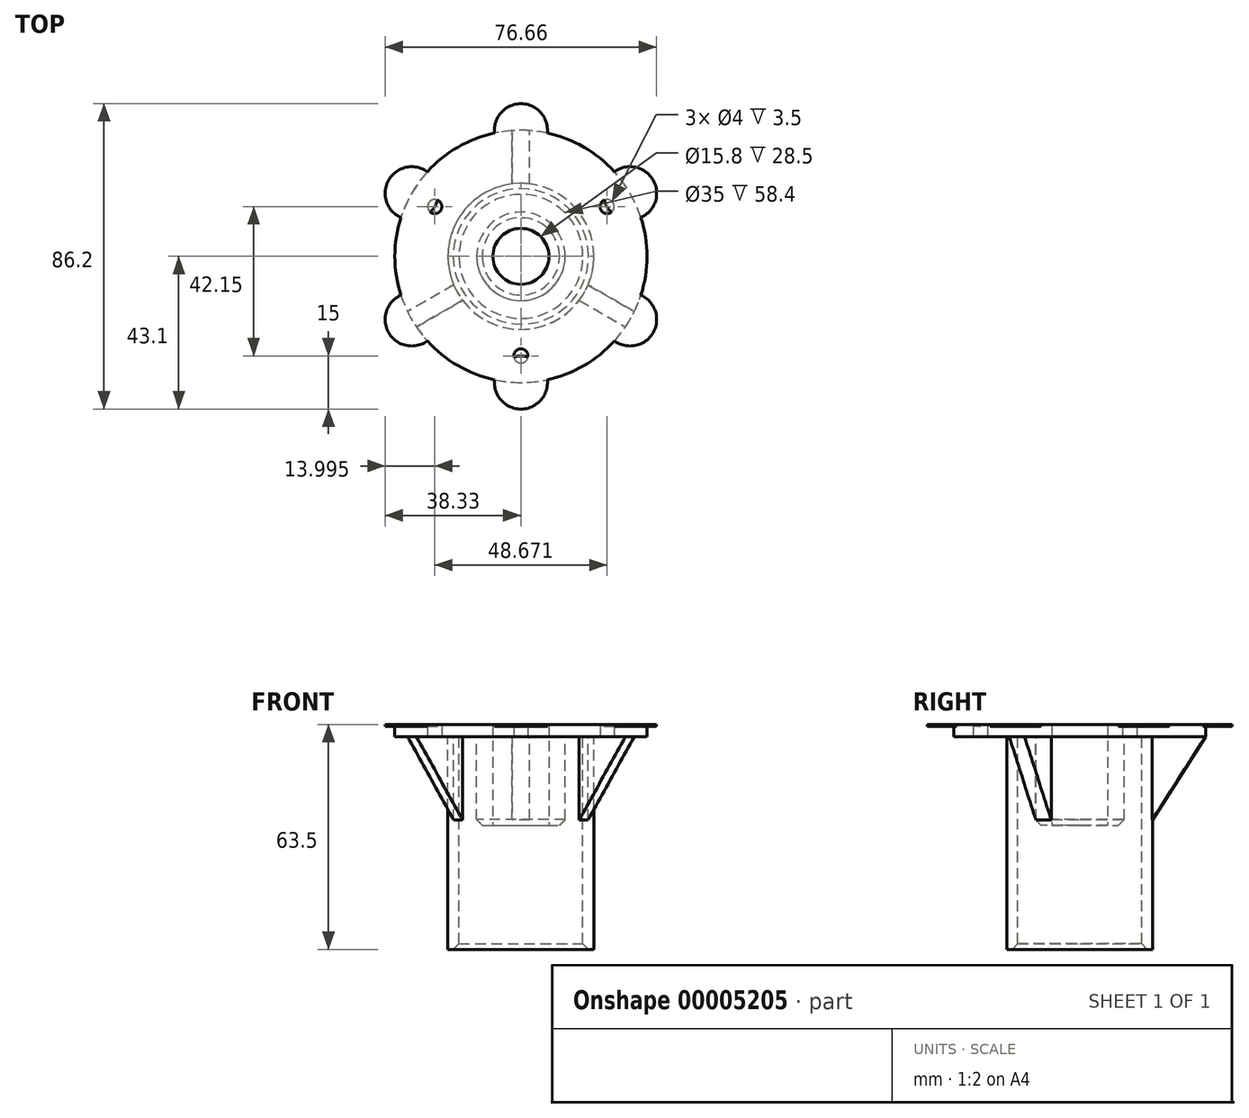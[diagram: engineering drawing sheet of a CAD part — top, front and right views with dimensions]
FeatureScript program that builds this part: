
annotation { "Feature Type Name" : "Feature", "Feature Type Description" : "" }
export const myFeature = defineFeature(function(context is Context, id is Id, definition is map)
    precondition{}
    {
        {
            var Q0;
            Q0=qCreatedBy(makeId("Front.planeOp"),FACE);
            var sketch = newSketch(context, id + "F0", { "sketchPlane" : qUnion([Q0])});
            skLineSegment(sketch, "E0", {"start": v(0, 36.77) * mm, "end": v(0, 0) * mm, "construction": true});
            skLineSegment(sketch, "E1", {"start": v(0, 0) * mm, "end": v(35.6, 0) * mm});
            skLineSegment(sketch, "E2", {"start": v(35.6, 0) * mm, "end": v(35.6, -3.5) * mm});
            skLineSegment(sketch, "E3", {"start": v(35.6, -3.5) * mm, "end": v(20.6, -3.5) * mm});
            skLineSegment(sketch, "E4", {"start": v(20.6, -3.5) * mm, "end": v(20.6, -63.5) * mm});
            skLineSegment(sketch, "E5", {"start": v(20.6, -63.5) * mm, "end": v(17.1, -63.5) * mm});
            skLineSegment(sketch, "E6", {"start": v(17.1, -63.5) * mm, "end": v(17.1, -3.5) * mm});
            skLineSegment(sketch, "E7", {"start": v(17.1, -3.5) * mm, "end": v(12.9, -3.5) * mm});
            skLineSegment(sketch, "E8", {"start": v(12.9, -3.5) * mm, "end": v(12.9, -28.5) * mm});
            skLineSegment(sketch, "E9", {"start": v(12.9, -28.5) * mm, "end": v(0, -28.5) * mm});
            skLineSegment(sketch, "E10", {"start": v(0, -28.5) * mm, "end": v(0, 0) * mm});
            skLineSegment(sketch, "E11", {"start": v(28.1, -3.5) * mm, "end": v(28.1, 0) * mm, "construction": true});
            skSolve(sketch);
        }
        {
            var Q0;
            Q0 = qSketchRegion(id + "F0", true);
            var Q1;
            Q1=sQuery(id+"F0.wireOp",EDGE,"E0");
            revolve(context, id + "F1", {"entities" : qUnion([Q0]), "axis" : qUnion([Q1]), "revolveType" : RevolveType.FULL});
        }
        {
            var Q0;
            Q0=makeQuery(id+"F1.opRevolve","SWEPT_EDGE",EDGE,{"disambiguationData":[OSD([sQuery(id+"F0.wireOp",EDGE,"E8"),sQuery(id+"F0.wireOp",EDGE,"E9")])]});
            var Q1;
            Q1=makeQuery(id+"F1.opRevolve","SWEPT_EDGE",EDGE,{"disambiguationData":[OSD([sQuery(id+"F0.wireOp",EDGE,"E5"),sQuery(id+"F0.wireOp",EDGE,"E6")])]});
            chamfer(context, id + "F2", {"entities" : qUnion([Q0, Q1]), "width" : 2 * mm, "tangentPropagation" : true});
        }
        {
            var Q0;
            Q0=makeQuery(id+"F1.opRevolve","SWEPT_FACE",FACE,{"disambiguationData":[OSD([sQuery(id+"F0.wireOp",EDGE,"E9")])]});
            var sketch = newSketch(context, id + "F3", { "sketchPlane" : qUnion([Q0])});
            skCircle(sketch, "E12", {"center": v(0, 0) * mm, "radius": 7.9 * mm});
            skSolve(sketch);
        }
        {
            var Q0;
            Q0 = qSketchRegion(id + "F3", true);
            extrude(context, id + "F4", {"entities" : qUnion([Q0]), "operationType" : NewBodyOperationType.REMOVE, "endBound" : BoundingType.THROUGH_ALL, "oppositeDirection" : true, "depth" : 25 * mm, "offsetDistance" : 25 * mm});
        }
        {
            var Q0;
            Q0=makeQuery(id+"F1.opRevolve","SWEPT_FACE",FACE,{"disambiguationData":[OSD([sQuery(id+"F0.wireOp",EDGE,"E3")])]});
            var sketch = newSketch(context, id + "F5", { "sketchPlane" : qUnion([Q0])});
            skLineSegment(sketch, "E13", {"start": v(0, 0) * mm, "end": v(0, 35.6) * mm, "construction": true});
            skCircle(sketch, "E14", {"center": v(0, 28.1) * mm, "radius": 2 * mm});
            skCircle(sketch, "E15.1.0", {"center": v(-24.34, -14.05) * mm, "radius": 2 * mm});
            skCircle(sketch, "E15.2.0", {"center": v(24.34, -14.05) * mm, "radius": 2 * mm});
            skPoint(sketch, "E15.center", {"position": v(0, 0) * mm});
            skSolve(sketch);
        }
        {
            var Q0;
            Q0 = qSketchRegion(id + "F5", true);
            extrude(context, id + "F6", {"entities" : qUnion([Q0]), "operationType" : NewBodyOperationType.REMOVE, "endBound" : BoundingType.THROUGH_ALL, "oppositeDirection" : true, "depth" : 25 * mm, "offsetDistance" : 25 * mm});
        }
        {
            var Q0;
            Q0=makeQuery(id+"F1.opRevolve","SWEPT_FACE",FACE,{"disambiguationData":[OSD([sQuery(id+"F0.wireOp",EDGE,"E3")])]});
            var sketch = newSketch(context, id + "F7", { "sketchPlane" : qUnion([Q0])});
            skCircle(sketch, "E16.0", {"center": v(0, 0) * mm, "radius": 20.6 * mm, "construction": true});
            skCircle(sketch, "E16.1", {"center": v(0, 0) * mm, "radius": 35.6 * mm, "construction": true});
            skLineSegment(sketch, "E17", {"start": v(0, 35.6) * mm, "end": v(0, 20.6) * mm, "construction": true});
            skLineSegment(sketch, "E18", {"start": v(0, -20.6) * mm, "end": v(0, -35.6) * mm, "construction": true});
            skLineSegment(sketch, "E19.bottom", {"start": v(-2.5, -20.45) * mm, "end": v(2.5, -20.45) * mm});
            skLineSegment(sketch, "E19.top", {"start": v(-2.5, -35.51) * mm, "end": v(2.5, -35.51) * mm, "construction": true});
            skLineSegment(sketch, "E19.left", {"start": v(-2.5, -20.45) * mm, "end": v(-2.5, -35.51) * mm});
            skLineSegment(sketch, "E19.right", {"start": v(2.5, -20.45) * mm, "end": v(2.5, -35.51) * mm});
            skArc(sketch, "E20", {"start": v(-2.5, -35.51) * mm, "mid": v(0, -35.6) * mm, "end": v(2.5, -35.51) * mm});
            skLineSegment(sketch, "E21.1.0", {"start": v(18.96, 8.06) * mm, "end": v(16.46, 12.39) * mm});
            skLineSegment(sketch, "E21.1.1", {"start": v(18.96, 8.06) * mm, "end": v(32, 15.6) * mm});
            skLineSegment(sketch, "E21.1.2", {"start": v(16.46, 12.39) * mm, "end": v(29.5, 19.92) * mm});
            skArc(sketch, "E21.1.3", {"start": v(32, 15.6) * mm, "mid": v(30.83, 17.8) * mm, "end": v(29.5, 19.92) * mm});
            skLineSegment(sketch, "E21.1.4", {"start": v(32, 15.6) * mm, "end": v(29.5, 19.92) * mm, "construction": true});
            skLineSegment(sketch, "E21.2.0", {"start": v(-16.46, 12.39) * mm, "end": v(-18.96, 8.06) * mm});
            skLineSegment(sketch, "E21.2.1", {"start": v(-16.46, 12.39) * mm, "end": v(-29.5, 19.92) * mm});
            skLineSegment(sketch, "E21.2.2", {"start": v(-18.96, 8.06) * mm, "end": v(-32, 15.6) * mm});
            skArc(sketch, "E21.2.3", {"start": v(-29.5, 19.92) * mm, "mid": v(-30.83, 17.8) * mm, "end": v(-32, 15.6) * mm});
            skLineSegment(sketch, "E21.2.4", {"start": v(-29.5, 19.92) * mm, "end": v(-32, 15.6) * mm, "construction": true});
            skSolve(sketch);
        }
        {
            var Q0;
            Q0 = qSketchRegion(id + "F7", true);
            extrude(context, id + "F8", {"entities" : qUnion([Q0]), "operationType" : NewBodyOperationType.ADD, "depth" : 25 * mm, "offsetDistance" : 25 * mm});
        }
        {
            var Q0;
            Q0=makeQuery(id+"F8.opExtrude","CAP_EDGE",EDGE,{"disambiguationData":[OSD([sQuery(id+"F7.wireOp",EDGE,"E21.2.3")])],"isStart":false});
            var Q1;
            Q1=makeQuery(id+"F8.opExtrude","CAP_EDGE",EDGE,{"disambiguationData":[OSD([sQuery(id+"F7.wireOp",EDGE,"E20")])],"isStart":false});
            var Q2;
            Q2=makeQuery(id+"F8.opExtrude","CAP_EDGE",EDGE,{"disambiguationData":[OSD([sQuery(id+"F7.wireOp",EDGE,"E21.1.3")])],"isStart":false});
            chamfer(context, id + "F9", {"entities" : qUnion([Q0, Q1, Q2]), "chamferType" : ChamferType.TWO_OFFSETS, "width1" : 25 * mm, "oppositeDirection" : false, "width2" : 16 * mm, "tangentPropagation" : true});
        }
        {
            var Q0;
            Q0=makeQuery(id+"F1.opRevolve","SWEPT_FACE",FACE,{"disambiguationData":[OSD([sQuery(id+"F0.wireOp",EDGE,"E7")])]});
            var sketch = newSketch(context, id + "F10", { "sketchPlane" : qUnion([Q0])});
            skCircle(sketch, "E22", {"center": v(0, 0) * mm, "radius": 12.5 * mm});
            skCircle(sketch, "E23", {"center": v(0, 0) * mm, "radius": 17.5 * mm});
            skSolve(sketch);
        }
        {
            var Q0;
            Q0 = qSketchRegion(id + "F10", true);
            extrude(context, id + "F11", {"entities" : qUnion([Q0]), "operationType" : NewBodyOperationType.REMOVE, "endBound" : BoundingType.THROUGH_ALL, "depth" : 25 * mm, "offsetDistance" : 25 * mm});
        }
        {
            var Q0;
            Q0=makeQuery(id+"F1.opRevolve","SWEPT_FACE",FACE,{"disambiguationData":[OSD([sQuery(id+"F0.wireOp",EDGE,"E1")])]});
            var sketch = newSketch(context, id + "F12", { "sketchPlane" : qUnion([Q0])});
            skLineSegment(sketch, "E24", {"start": v(0, 0) * mm, "end": v(0, 35.6) * mm, "construction": true});
            skCircle(sketch, "E25", {"center": v(0, 35.6) * mm, "radius": 7.5 * mm});
            skCircle(sketch, "E26.1.0", {"center": v(-30.83, 17.8) * mm, "radius": 7.5 * mm});
            skCircle(sketch, "E26.2.0", {"center": v(-30.83, -17.8) * mm, "radius": 7.5 * mm});
            skPoint(sketch, "E26.center", {"position": v(0, 0) * mm});
            skCircle(sketch, "E27.1.3.0", {"center": v(0, -35.6) * mm, "radius": 7.5 * mm});
            skCircle(sketch, "E27.1.4.0", {"center": v(30.83, -17.8) * mm, "radius": 7.5 * mm});
            skCircle(sketch, "E27.1.5.0", {"center": v(30.83, 17.8) * mm, "radius": 7.5 * mm});
            skSolve(sketch);
        }
        {
            var Q0;
            Q0 = qSketchRegion(id + "F12", true);
            extrude(context, id + "F13", {"entities" : qUnion([Q0]), "operationType" : NewBodyOperationType.ADD, "oppositeDirection" : true, "depth" : 0.5 * mm, "offsetDistance" : 25 * mm});
        }
    });
